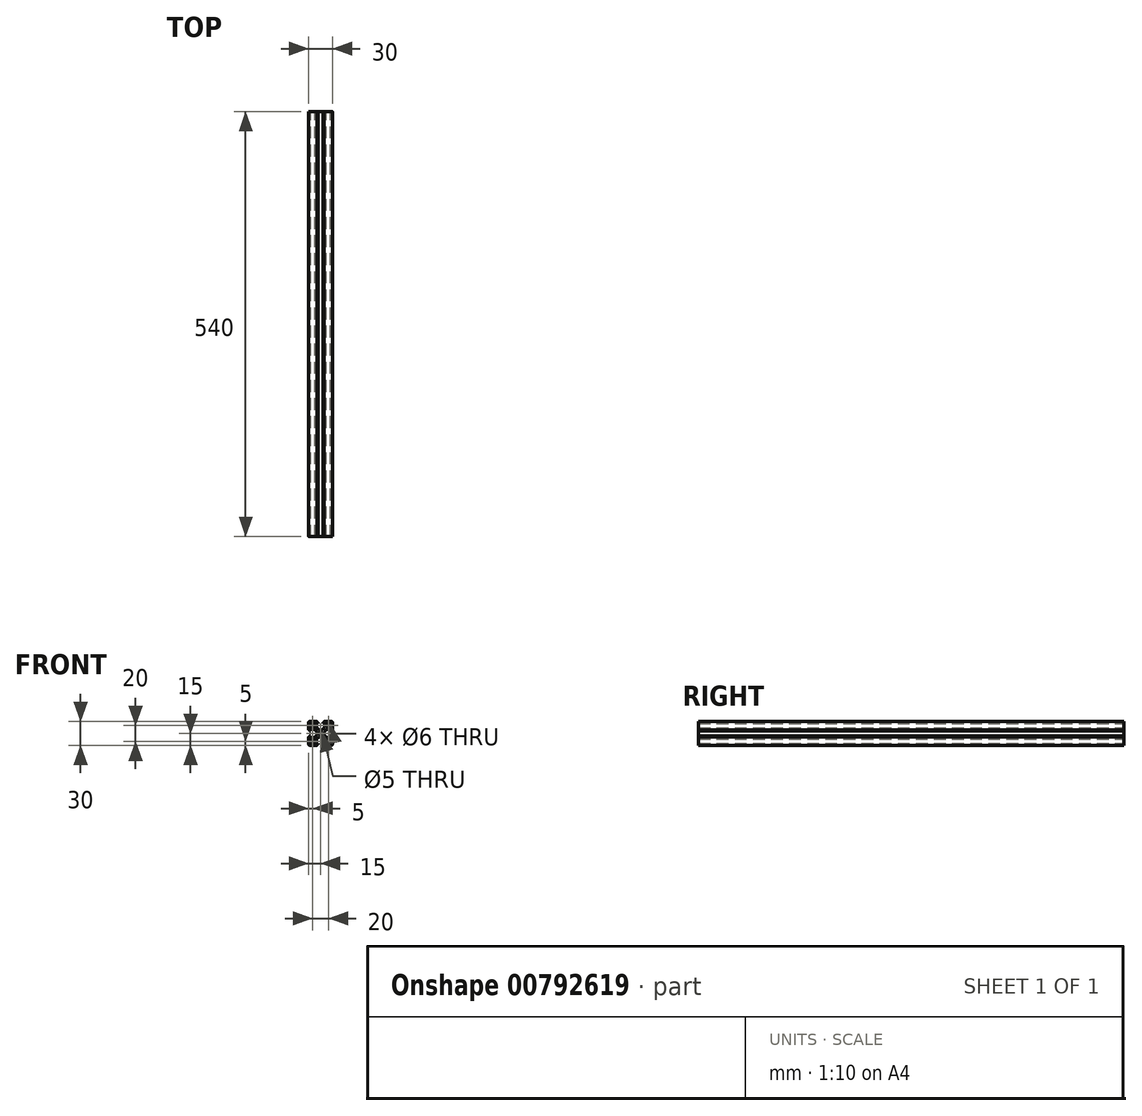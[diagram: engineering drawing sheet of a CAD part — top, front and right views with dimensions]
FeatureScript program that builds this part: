
annotation { "Feature Type Name" : "Feature", "Feature Type Description" : "" }
export const myFeature = defineFeature(function(context is Context, id is Id, definition is map)
    precondition{}
    {
        {
            var Q0;
            Q0=qCreatedBy(makeId("Front.planeOp"),FACE);
            var sketch = newSketch(context, id + "F0", { "sketchPlane" : qUnion([Q0])});
            skCircle(sketch, "E0", {"center": v(0, 0) * mm, "radius": 2.5 * mm});
            skCircle(sketch, "E1", {"center": v(-10, 10) * mm, "radius": 3 * mm});
            skCircle(sketch, "E2", {"center": v(10, 10) * mm, "radius": 3 * mm});
            skCircle(sketch, "E3", {"center": v(10, -10) * mm, "radius": 3 * mm});
            skCircle(sketch, "E4", {"center": v(-10, -10) * mm, "radius": 3 * mm});
            skLineSegment(sketch, "E5.bottom", {"start": v(-14, 15) * mm, "end": v(-4.5, 15) * mm});
            skLineSegment(sketch, "E5.top", {"start": v(-14, -15) * mm, "end": v(-4.2, -15) * mm});
            skLineSegment(sketch, "E5.left", {"start": v(-15, 14) * mm, "end": v(-15, 4.2) * mm});
            skLineSegment(sketch, "E5.right", {"start": v(15, 14) * mm, "end": v(15, 4.2) * mm});
            skPoint(sketch, "E6.visualSharp", {"position": v(-15, 15) * mm});
            skArc(sketch, "E6.filletArc", {"start": v(-14, 15) * mm, "mid": v(-14.7, 14.7) * mm, "end": v(-15, 14) * mm});
            skPoint(sketch, "E7.visualSharp", {"position": v(-15, -15) * mm});
            skArc(sketch, "E7.filletArc", {"start": v(-15, -14) * mm, "mid": v(-14.7, -14.7) * mm, "end": v(-14, -15) * mm});
            skPoint(sketch, "E8.visualSharp", {"position": v(15, -15) * mm});
            skArc(sketch, "E8.filletArc", {"start": v(14, -15) * mm, "mid": v(14.7, -14.7) * mm, "end": v(15, -14) * mm});
            skPoint(sketch, "E9.visualSharp", {"position": v(15, 15) * mm});
            skArc(sketch, "E9.filletArc", {"start": v(15, 14) * mm, "mid": v(14.7, 14.7) * mm, "end": v(14, 15) * mm});
            skLineSegment(sketch, "E10", {"start": v(-3.25, 13.7) * mm, "end": v(-3.25, 12.5) * mm});
            skLineSegment(sketch, "E11", {"start": v(-3.25, 12.5) * mm, "end": v(-5.25, 12.5) * mm});
            skLineSegment(sketch, "E12", {"start": v(-5.25, 12.5) * mm, "end": v(-5.25, 8) * mm});
            skLineSegment(sketch, "E13", {"start": v(-4.97, 7.3) * mm, "end": v(-2.54, 4.8) * mm});
            skLineSegment(sketch, "E14", {"start": v(-1.83, 4.5) * mm, "end": v(1.83, 4.5) * mm});
            skLineSegment(sketch, "E15", {"start": v(2.54, 4.8) * mm, "end": v(4.97, 7.3) * mm});
            skLineSegment(sketch, "E16", {"start": v(5.25, 8) * mm, "end": v(5.25, 12.5) * mm});
            skLineSegment(sketch, "E17", {"start": v(5.25, 12.5) * mm, "end": v(3.25, 12.5) * mm});
            skLineSegment(sketch, "E18", {"start": v(3.25, 12.5) * mm, "end": v(3.25, 13.7) * mm});
            skLineSegment(sketch, "E19.trimOffspring", {"start": v(4.5, 15) * mm, "end": v(14, 15) * mm});
            skPoint(sketch, "E20.visualSharp", {"position": v(-5.25, 7.6) * mm});
            skArc(sketch, "E20.filletArc", {"start": v(-5.25, 8) * mm, "mid": v(-5.18, 7.63) * mm, "end": v(-4.97, 7.3) * mm});
            skPoint(sketch, "E21.visualSharp", {"position": v(-2.25, 4.5) * mm});
            skArc(sketch, "E21.filletArc", {"start": v(-2.54, 4.8) * mm, "mid": v(-2.22, 4.58) * mm, "end": v(-1.83, 4.5) * mm});
            skPoint(sketch, "E22.visualSharp", {"position": v(2.25, 4.5) * mm});
            skArc(sketch, "E22.filletArc", {"start": v(1.83, 4.5) * mm, "mid": v(2.22, 4.58) * mm, "end": v(2.54, 4.8) * mm});
            skPoint(sketch, "E23.visualSharp", {"position": v(5.25, 7.6) * mm});
            skArc(sketch, "E23.filletArc", {"start": v(4.97, 7.3) * mm, "mid": v(5.18, 7.63) * mm, "end": v(5.25, 8) * mm});
            skLineSegment(sketch, "E24", {"start": v(-3.55, 14) * mm, "end": v(-3.7, 14) * mm});
            skLineSegment(sketch, "E25", {"start": v(-4.2, 14.5) * mm, "end": v(-4.2, 14.7) * mm});
            skLineSegment(sketch, "E26", {"start": v(3.55, 14) * mm, "end": v(3.7, 14) * mm});
            skLineSegment(sketch, "E27", {"start": v(4.2, 14.5) * mm, "end": v(4.2, 14.7) * mm});
            skPoint(sketch, "E28.visualSharp", {"position": v(-4.2, 15) * mm});
            skArc(sketch, "E28.filletArc", {"start": v(-4.2, 14.7) * mm, "mid": v(-4.29, 14.91) * mm, "end": v(-4.5, 15) * mm});
            skPoint(sketch, "E29.visualSharp", {"position": v(-3.25, 14) * mm});
            skArc(sketch, "E29.filletArc", {"start": v(-3.25, 13.7) * mm, "mid": v(-3.34, 13.91) * mm, "end": v(-3.55, 14) * mm});
            skPoint(sketch, "E30.visualSharp", {"position": v(3.25, 14) * mm});
            skArc(sketch, "E30.filletArc", {"start": v(3.55, 14) * mm, "mid": v(3.34, 13.91) * mm, "end": v(3.25, 13.7) * mm});
            skPoint(sketch, "E31.visualSharp", {"position": v(4.2, 15) * mm});
            skArc(sketch, "E31.filletArc", {"start": v(4.5, 15) * mm, "mid": v(4.29, 14.91) * mm, "end": v(4.2, 14.7) * mm});
            skPoint(sketch, "E32.visualSharp", {"position": v(4.2, 14) * mm});
            skArc(sketch, "E32.filletArc", {"start": v(3.7, 14) * mm, "mid": v(4.05, 14.15) * mm, "end": v(4.2, 14.5) * mm});
            skPoint(sketch, "E33.visualSharp", {"position": v(-4.2, 14) * mm});
            skArc(sketch, "E33.filletArc", {"start": v(-4.2, 14.5) * mm, "mid": v(-4.05, 14.15) * mm, "end": v(-3.7, 14) * mm});
            skPoint(sketch, "E34.1.0", {"position": v(-14, 3.25) * mm});
            skLineSegment(sketch, "E34.1.1", {"start": v(-12.5, -3.25) * mm, "end": v(-12.5, -5.25) * mm});
            skPoint(sketch, "E34.1.2", {"position": v(-15, 4.2) * mm});
            skPoint(sketch, "E34.1.3", {"position": v(-14, 4.2) * mm});
            skLineSegment(sketch, "E34.1.4", {"start": v(-12.5, -5.25) * mm, "end": v(-8, -5.25) * mm});
            skLineSegment(sketch, "E34.1.5", {"start": v(-4.8, 2.54) * mm, "end": v(-7.3, 4.97) * mm});
            skLineSegment(sketch, "E34.1.6", {"start": v(-12.5, 5.25) * mm, "end": v(-12.5, 3.25) * mm});
            skPoint(sketch, "E34.1.7", {"position": v(-15, -4.2) * mm});
            skPoint(sketch, "E34.1.8", {"position": v(-7.6, -5.25) * mm});
            skLineSegment(sketch, "E34.1.9", {"start": v(-8, 5.25) * mm, "end": v(-12.5, 5.25) * mm});
            skPoint(sketch, "E34.1.10", {"position": v(-14, -3.25) * mm});
            skPoint(sketch, "E34.1.11", {"position": v(-7.6, 5.25) * mm});
            skLineSegment(sketch, "E34.1.12", {"start": v(-4.5, -1.83) * mm, "end": v(-4.5, 1.83) * mm});
            skPoint(sketch, "E34.1.13", {"position": v(-4.5, 2.25) * mm});
            skPoint(sketch, "E34.1.14", {"position": v(-4.5, -2.25) * mm});
            skPoint(sketch, "E34.1.15", {"position": v(-14, -4.2) * mm});
            skLineSegment(sketch, "E34.1.16", {"start": v(-12.5, 3.25) * mm, "end": v(-13.7, 3.25) * mm});
            skLineSegment(sketch, "E34.1.17", {"start": v(-7.3, -4.97) * mm, "end": v(-4.8, -2.54) * mm});
            skLineSegment(sketch, "E34.1.18", {"start": v(-13.7, -3.25) * mm, "end": v(-12.5, -3.25) * mm});
            skArc(sketch, "E34.1.19", {"start": v(-14.5, -4.2) * mm, "mid": v(-14.15, -4.05) * mm, "end": v(-14, -3.7) * mm});
            skArc(sketch, "E34.1.20", {"start": v(-4.5, 1.83) * mm, "mid": v(-4.58, 2.22) * mm, "end": v(-4.8, 2.54) * mm});
            skArc(sketch, "E34.1.21", {"start": v(-8, -5.25) * mm, "mid": v(-7.63, -5.18) * mm, "end": v(-7.3, -4.97) * mm});
            skArc(sketch, "E34.1.22", {"start": v(-4.8, -2.54) * mm, "mid": v(-4.58, -2.22) * mm, "end": v(-4.5, -1.83) * mm});
            skArc(sketch, "E34.1.23", {"start": v(-7.3, 4.97) * mm, "mid": v(-7.63, 5.18) * mm, "end": v(-8, 5.25) * mm});
            skArc(sketch, "E34.1.24", {"start": v(-14, 3.55) * mm, "mid": v(-13.91, 3.34) * mm, "end": v(-13.7, 3.25) * mm});
            skLineSegment(sketch, "E34.1.25", {"start": v(-14, -3.55) * mm, "end": v(-14, -3.7) * mm});
            skArc(sketch, "E34.1.26", {"start": v(-14, 3.7) * mm, "mid": v(-14.15, 4.05) * mm, "end": v(-14.5, 4.2) * mm});
            skArc(sketch, "E34.1.27", {"start": v(-14.7, -4.2) * mm, "mid": v(-14.91, -4.29) * mm, "end": v(-15, -4.5) * mm});
            skArc(sketch, "E34.1.28", {"start": v(-13.7, -3.25) * mm, "mid": v(-13.91, -3.34) * mm, "end": v(-14, -3.55) * mm});
            skArc(sketch, "E34.1.29", {"start": v(-15, 4.5) * mm, "mid": v(-14.91, 4.29) * mm, "end": v(-14.7, 4.2) * mm});
            skLineSegment(sketch, "E34.1.30", {"start": v(-14.5, 4.2) * mm, "end": v(-14.7, 4.2) * mm});
            skLineSegment(sketch, "E34.1.31", {"start": v(-14.5, -4.2) * mm, "end": v(-14.7, -4.2) * mm});
            skLineSegment(sketch, "E34.1.32", {"start": v(-14, 3.55) * mm, "end": v(-14, 3.7) * mm});
            skPoint(sketch, "E34.2.0", {"position": v(-3.25, -14) * mm});
            skLineSegment(sketch, "E34.2.1", {"start": v(3.25, -12.5) * mm, "end": v(5.25, -12.5) * mm});
            skPoint(sketch, "E34.2.2", {"position": v(-4.2, -15) * mm});
            skPoint(sketch, "E34.2.3", {"position": v(-4.2, -14) * mm});
            skLineSegment(sketch, "E34.2.4", {"start": v(5.25, -12.5) * mm, "end": v(5.25, -8) * mm});
            skLineSegment(sketch, "E34.2.5", {"start": v(-2.54, -4.8) * mm, "end": v(-4.97, -7.3) * mm});
            skLineSegment(sketch, "E34.2.6", {"start": v(-5.25, -12.5) * mm, "end": v(-3.25, -12.5) * mm});
            skPoint(sketch, "E34.2.7", {"position": v(4.2, -15) * mm});
            skPoint(sketch, "E34.2.8", {"position": v(5.25, -7.6) * mm});
            skLineSegment(sketch, "E34.2.9", {"start": v(-5.25, -8) * mm, "end": v(-5.25, -12.5) * mm});
            skPoint(sketch, "E34.2.10", {"position": v(3.25, -14) * mm});
            skPoint(sketch, "E34.2.11", {"position": v(-5.25, -7.6) * mm});
            skLineSegment(sketch, "E34.2.12", {"start": v(1.83, -4.5) * mm, "end": v(-1.83, -4.5) * mm});
            skPoint(sketch, "E34.2.13", {"position": v(-2.25, -4.5) * mm});
            skPoint(sketch, "E34.2.14", {"position": v(2.25, -4.5) * mm});
            skPoint(sketch, "E34.2.15", {"position": v(4.2, -14) * mm});
            skLineSegment(sketch, "E34.2.16", {"start": v(-3.25, -12.5) * mm, "end": v(-3.25, -13.7) * mm});
            skLineSegment(sketch, "E34.2.17", {"start": v(4.97, -7.3) * mm, "end": v(2.54, -4.8) * mm});
            skLineSegment(sketch, "E34.2.18", {"start": v(3.25, -13.7) * mm, "end": v(3.25, -12.5) * mm});
            skArc(sketch, "E34.2.19", {"start": v(4.2, -14.5) * mm, "mid": v(4.05, -14.15) * mm, "end": v(3.7, -14) * mm});
            skArc(sketch, "E34.2.20", {"start": v(-1.83, -4.5) * mm, "mid": v(-2.22, -4.58) * mm, "end": v(-2.54, -4.8) * mm});
            skArc(sketch, "E34.2.21", {"start": v(5.25, -8) * mm, "mid": v(5.18, -7.63) * mm, "end": v(4.97, -7.3) * mm});
            skArc(sketch, "E34.2.22", {"start": v(2.54, -4.8) * mm, "mid": v(2.22, -4.58) * mm, "end": v(1.83, -4.5) * mm});
            skArc(sketch, "E34.2.23", {"start": v(-4.97, -7.3) * mm, "mid": v(-5.18, -7.63) * mm, "end": v(-5.25, -8) * mm});
            skArc(sketch, "E34.2.24", {"start": v(-3.55, -14) * mm, "mid": v(-3.34, -13.91) * mm, "end": v(-3.25, -13.7) * mm});
            skLineSegment(sketch, "E34.2.25", {"start": v(3.55, -14) * mm, "end": v(3.7, -14) * mm});
            skArc(sketch, "E34.2.26", {"start": v(-3.7, -14) * mm, "mid": v(-4.05, -14.15) * mm, "end": v(-4.2, -14.5) * mm});
            skArc(sketch, "E34.2.27", {"start": v(4.2, -14.7) * mm, "mid": v(4.29, -14.91) * mm, "end": v(4.5, -15) * mm});
            skArc(sketch, "E34.2.28", {"start": v(3.25, -13.7) * mm, "mid": v(3.34, -13.91) * mm, "end": v(3.55, -14) * mm});
            skArc(sketch, "E34.2.29", {"start": v(-4.5, -15) * mm, "mid": v(-4.29, -14.91) * mm, "end": v(-4.2, -14.7) * mm});
            skLineSegment(sketch, "E34.2.30", {"start": v(-4.2, -14.5) * mm, "end": v(-4.2, -14.7) * mm});
            skLineSegment(sketch, "E34.2.31", {"start": v(4.2, -14.5) * mm, "end": v(4.2, -14.7) * mm});
            skLineSegment(sketch, "E34.2.32", {"start": v(-3.55, -14) * mm, "end": v(-3.7, -14) * mm});
            skPoint(sketch, "E34.3.0", {"position": v(14, -3.25) * mm});
            skLineSegment(sketch, "E34.3.1", {"start": v(12.5, 3.25) * mm, "end": v(12.5, 5.25) * mm});
            skPoint(sketch, "E34.3.2", {"position": v(15, -4.2) * mm});
            skPoint(sketch, "E34.3.3", {"position": v(14, -4.2) * mm});
            skLineSegment(sketch, "E34.3.4", {"start": v(12.5, 5.25) * mm, "end": v(8, 5.25) * mm});
            skLineSegment(sketch, "E34.3.5", {"start": v(4.8, -2.54) * mm, "end": v(7.3, -4.97) * mm});
            skLineSegment(sketch, "E34.3.6", {"start": v(12.5, -5.25) * mm, "end": v(12.5, -3.25) * mm});
            skPoint(sketch, "E34.3.7", {"position": v(15, 4.2) * mm});
            skPoint(sketch, "E34.3.8", {"position": v(7.6, 5.25) * mm});
            skLineSegment(sketch, "E34.3.9", {"start": v(8, -5.25) * mm, "end": v(12.5, -5.25) * mm});
            skPoint(sketch, "E34.3.10", {"position": v(14, 3.25) * mm});
            skPoint(sketch, "E34.3.11", {"position": v(7.6, -5.25) * mm});
            skLineSegment(sketch, "E34.3.12", {"start": v(4.5, 1.83) * mm, "end": v(4.5, -1.83) * mm});
            skPoint(sketch, "E34.3.13", {"position": v(4.5, -2.25) * mm});
            skPoint(sketch, "E34.3.14", {"position": v(4.5, 2.25) * mm});
            skPoint(sketch, "E34.3.15", {"position": v(14, 4.2) * mm});
            skLineSegment(sketch, "E34.3.16", {"start": v(12.5, -3.25) * mm, "end": v(13.7, -3.25) * mm});
            skLineSegment(sketch, "E34.3.17", {"start": v(7.3, 4.97) * mm, "end": v(4.8, 2.54) * mm});
            skLineSegment(sketch, "E34.3.18", {"start": v(13.7, 3.25) * mm, "end": v(12.5, 3.25) * mm});
            skArc(sketch, "E34.3.19", {"start": v(14.5, 4.2) * mm, "mid": v(14.15, 4.05) * mm, "end": v(14, 3.7) * mm});
            skArc(sketch, "E34.3.20", {"start": v(4.5, -1.83) * mm, "mid": v(4.58, -2.22) * mm, "end": v(4.8, -2.54) * mm});
            skArc(sketch, "E34.3.21", {"start": v(8, 5.25) * mm, "mid": v(7.63, 5.18) * mm, "end": v(7.3, 4.97) * mm});
            skArc(sketch, "E34.3.22", {"start": v(4.8, 2.54) * mm, "mid": v(4.58, 2.22) * mm, "end": v(4.5, 1.83) * mm});
            skArc(sketch, "E34.3.23", {"start": v(7.3, -4.97) * mm, "mid": v(7.63, -5.18) * mm, "end": v(8, -5.25) * mm});
            skArc(sketch, "E34.3.24", {"start": v(14, -3.55) * mm, "mid": v(13.91, -3.34) * mm, "end": v(13.7, -3.25) * mm});
            skLineSegment(sketch, "E34.3.25", {"start": v(14, 3.55) * mm, "end": v(14, 3.7) * mm});
            skArc(sketch, "E34.3.26", {"start": v(14, -3.7) * mm, "mid": v(14.15, -4.05) * mm, "end": v(14.5, -4.2) * mm});
            skArc(sketch, "E34.3.27", {"start": v(14.7, 4.2) * mm, "mid": v(14.91, 4.29) * mm, "end": v(15, 4.5) * mm});
            skArc(sketch, "E34.3.28", {"start": v(13.7, 3.25) * mm, "mid": v(13.91, 3.34) * mm, "end": v(14, 3.55) * mm});
            skArc(sketch, "E34.3.29", {"start": v(15, -4.5) * mm, "mid": v(14.91, -4.29) * mm, "end": v(14.7, -4.2) * mm});
            skLineSegment(sketch, "E34.3.30", {"start": v(14.5, -4.2) * mm, "end": v(14.7, -4.2) * mm});
            skLineSegment(sketch, "E34.3.31", {"start": v(14.5, 4.2) * mm, "end": v(14.7, 4.2) * mm});
            skLineSegment(sketch, "E34.3.32", {"start": v(14, -3.55) * mm, "end": v(14, -3.7) * mm});
            skLineSegment(sketch, "E35.trimOffspring", {"start": v(-15, -4.2) * mm, "end": v(-15, -14) * mm});
            skLineSegment(sketch, "E36.trimOffspring", {"start": v(15, -4.2) * mm, "end": v(15, -14) * mm});
            skLineSegment(sketch, "E37.trimOffspring", {"start": v(4.2, -15) * mm, "end": v(14, -15) * mm});
            skSolve(sketch);
        }
        {
            var Q0;
            Q0=makeQuery(id+"F0.imprint","IMPRINT",FACE,{"disambiguationData":[TD([[makeQuery(id+"F0.imprint","IMPRINT",EDGE,{"derivedFrom":sQuery(id+"F0.wireOp",EDGE,"E0")}),-1.0]])]});
            extrude(context, id + "F1", {"entities" : qUnion([Q0]), "depth" : 540 * mm, "offsetDistance" : 25 * mm});
        }
    });
